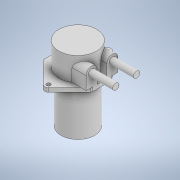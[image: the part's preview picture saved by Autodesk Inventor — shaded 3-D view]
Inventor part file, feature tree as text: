
AUTODESK INVENTOR PART (.ipt)
format: ipt  version: 2022 (Build 260153000, 153)  size: 188,416 bytes
history: native  units: mm
features: extrude x5, sketch x5, projected_geometry x1
ambient origin geometry x8: Origin, YZ Plane, XZ Plane, XY Plane, X Axis, Y Axis, Z Axis, Center Point
bodies: Solid1 (feature_tree)
feature tree (11):
  extrude  "Extrusion1"  Depth=38.2mm TaperAngle=0.0deg
  extrude  "Extrusion2"  Depth=17.0mm
  extrude  "Extrusion3"  Depth=1.5mm
  extrude  "Extrusion4"  Depth=2.0mm
  extrude  "Extrusion5"  Depth=20.0mm
  sketch  "Sketch1"  dims[d0=27.6mm d1=38.2mm d2=0.0mm]
  sketch  "Sketch2"  dims[d3=39.7mm d4=17.0mm]
  sketch  "Sketch3"  dims[d6=3.2mm d7=1.5mm]
  sketch  "Sketch4"  dims[d8=27.25mm d9=2.0mm]
  projected_geometry  "Projected Loop1"
  sketch  "Sketch5"  dims[d10=3.3mm d11=0.0mm d12=31.0mm d13=19.5mm d14=0.0mm d15=8.0mm d16=15.2mm d17=9.1mm d18=15.2mm d19=0.0mm d20=5.2mm d21=5.2mm d22=20.0mm d23=0.0mm]
